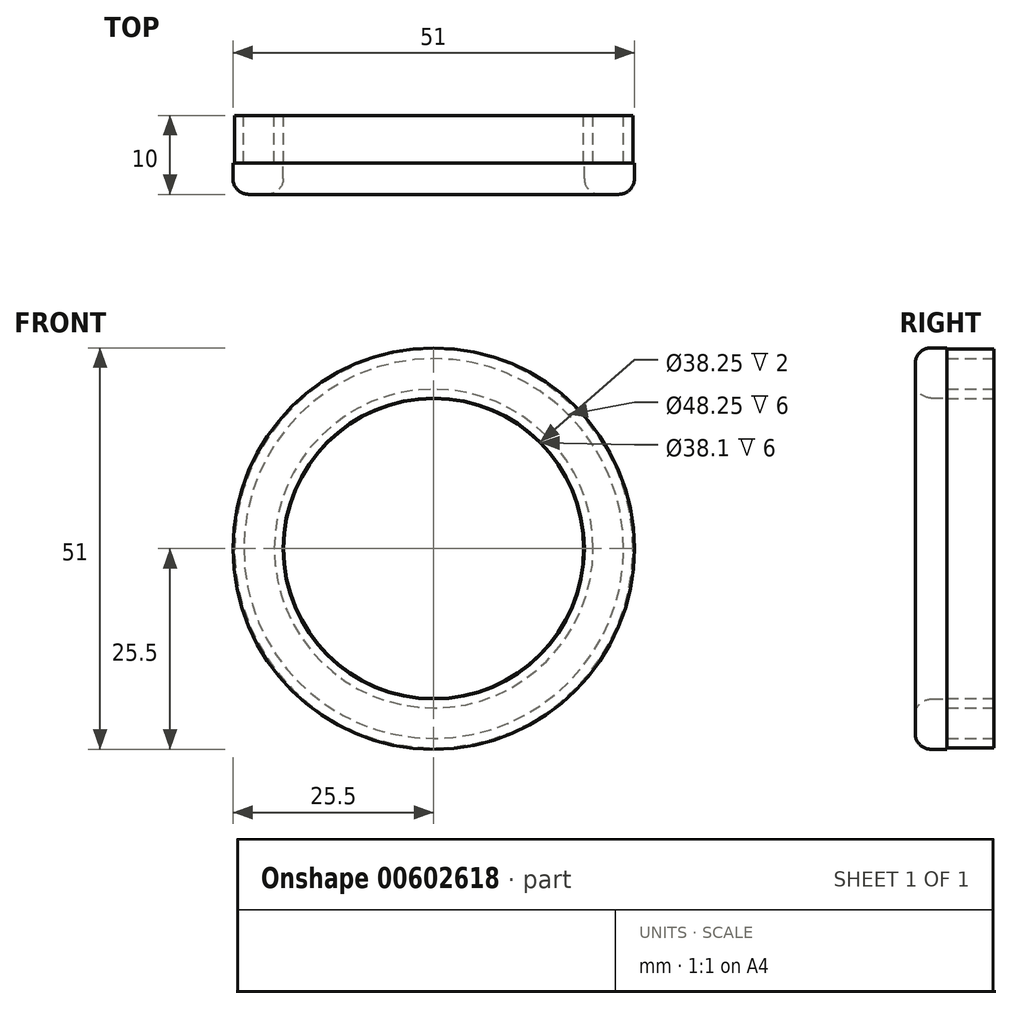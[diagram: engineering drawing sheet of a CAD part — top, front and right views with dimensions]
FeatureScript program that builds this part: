
annotation { "Feature Type Name" : "Feature", "Feature Type Description" : "" }
export const myFeature = defineFeature(function(context is Context, id is Id, definition is map)
    precondition{}
    {
        {
            var Q0;
            Q0=qCreatedBy(makeId("Front.planeOp"),FACE);
            var sketch = newSketch(context, id + "F0", { "sketchPlane" : qUnion([Q0])});
            skCircle(sketch, "E0", {"center": v(0, 0) * mm, "radius": 24.12 * mm});
            skCircle(sketch, "E1", {"center": v(0, 0) * mm, "radius": 20.25 * mm});
            skCircle(sketch, "E2", {"center": v(0, 0) * mm, "radius": 25.32 * mm});
            skCircle(sketch, "E3", {"center": v(0, 0) * mm, "radius": 19.05 * mm});
            skSolve(sketch);
        }
        {
            var Q0;
            Q0=makeQuery(id+"F0.imprint","IMPRINT",FACE,{"disambiguationData":[TD([[makeQuery(id+"F0.imprint","IMPRINT",EDGE,{"derivedFrom":sQuery(id+"F0.wireOp",EDGE,"E0")}),-1.0]])]});
            var Q1;
            Q1=makeQuery(id+"F0.imprint","IMPRINT",FACE,{"disambiguationData":[TD([[makeQuery(id+"F0.imprint","IMPRINT",EDGE,{"derivedFrom":sQuery(id+"F0.wireOp",EDGE,"E1")}),1.0]])]});
            extrude(context, id + "F1", {"entities" : qUnion([Q0, Q1]), "depth" : 6 * mm, "offsetDistance" : 25 * mm});
        }
        {
            var Q0;
            Q0=qCreatedBy(makeId("Front.planeOp"),FACE);
            cPlane(context, id + "F2", {"entities" : qUnion([Q0]), "cplaneType" : CPlaneType.OFFSET, "offset" : 6 * mm, "width" : 150 * mm, "height" : 150 * mm});
        }
        {
            var Q0;
            Q0=qCreatedBy(id+"F2.planeOp",FACE);
            var sketch = newSketch(context, id + "F3", { "sketchPlane" : qUnion([Q0])});
            skCircle(sketch, "E4", {"center": v(0, 0) * mm, "radius": 25.5 * mm});
            skCircle(sketch, "E5", {"center": v(0, 0) * mm, "radius": 19.12 * mm});
            skSolve(sketch);
        }
        {
            var Q0;
            Q0=makeQuery(id+"F3.imprint","IMPRINT",FACE,{"disambiguationData":[TD([[makeQuery(id+"F3.imprint","IMPRINT",EDGE,{"derivedFrom":sQuery(id+"F3.wireOp",EDGE,"E4")}),1.0]])]});
            var Q1;
            Q1=sQuery(id+"F3.wireOp",EDGE,"E4");
            extrude(context, id + "F4", {"entities" : qUnion([Q0]), "surfaceEntities" : qUnion([Q1]), "depth" : 4 * mm, "offsetDistance" : 25 * mm});
        }
        {
            var Q0;
            Q0=makeQuery(id+"F4.opExtrude","CAP_EDGE",EDGE,{"disambiguationData":[OSD([sQuery(id+"F3.wireOp",EDGE,"E4")])],"isStart":false});
            var Q1;
            Q1=makeQuery(id+"F4.opExtrude","CAP_EDGE",EDGE,{"disambiguationData":[OSD([sQuery(id+"F3.wireOp",EDGE,"E5")])],"isStart":false});
            fillet(context, id + "F5", {"entities" : qUnion([Q0, Q1]), "radius" : 2 * mm, "tangentPropagation" : true, "allowEdgeOverflow" : false});
        }
    });
